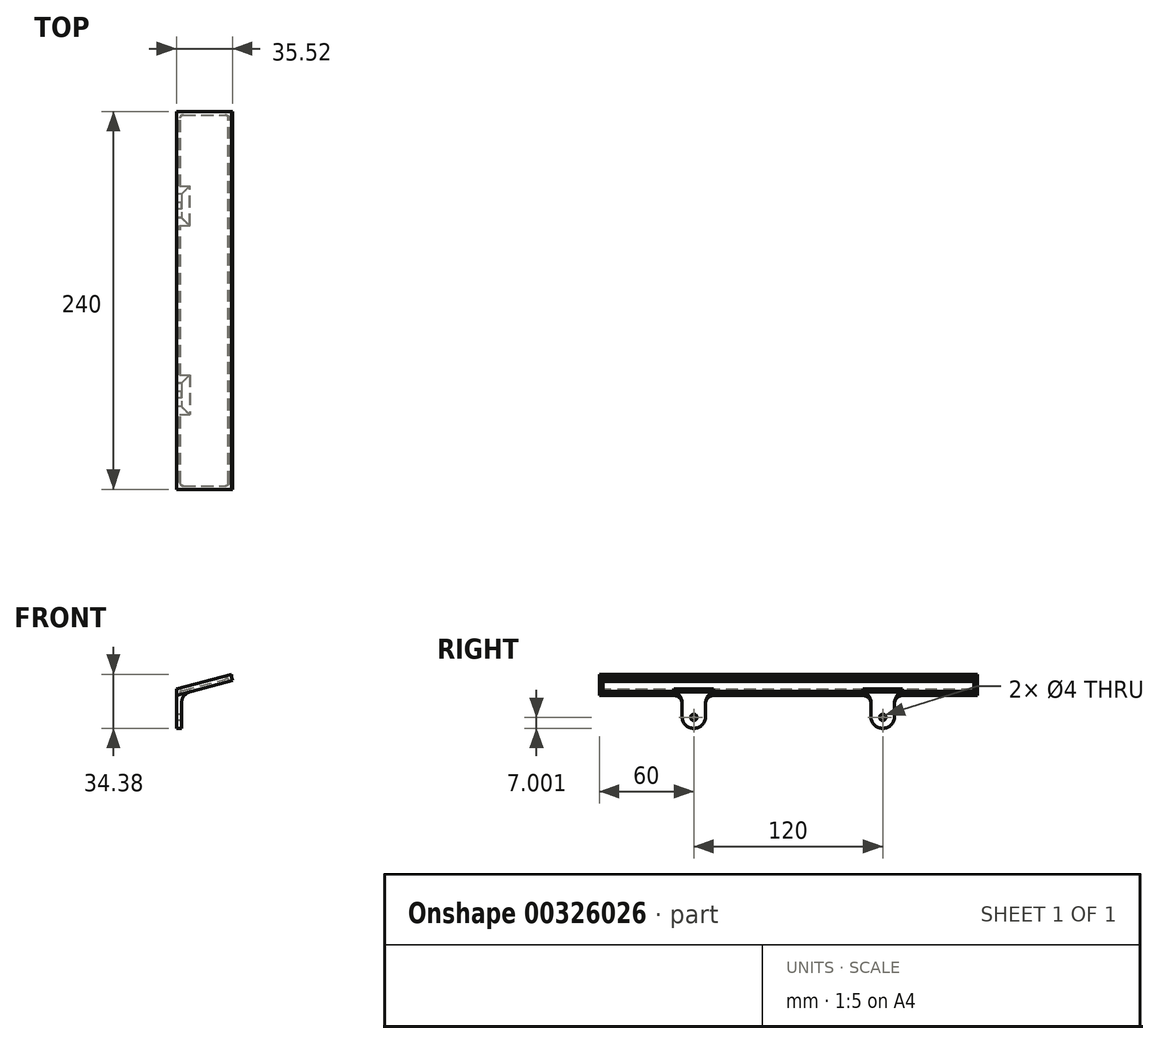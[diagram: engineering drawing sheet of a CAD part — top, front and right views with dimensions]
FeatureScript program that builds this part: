
annotation { "Feature Type Name" : "Feature", "Feature Type Description" : "" }
export const myFeature = defineFeature(function(context is Context, id is Id, definition is map)
    precondition{}
    {
        {
            assignVariable(context, id + "F0", {"name" : "Nozzle", "anyValue" : 1.1});
        }
        {
            var Q0;
            Q0=qCreatedBy(makeId("Front.planeOp"),FACE);
            var sketch = newSketch(context, id + "F1", { "sketchPlane" : qUnion([Q0])});
            skLineSegment(sketch, "E0", {"start": v(0, 2.07) * mm, "end": v(0, 0) * mm});
            skLineSegment(sketch, "E1", {"start": v(0, 0) * mm, "end": v(35, 9.38) * mm});
            skLineSegment(sketch, "E2", {"start": v(35, 9.38) * mm, "end": v(35, 11.45) * mm});
            skLineSegment(sketch, "E3", {"start": v(35, 11.45) * mm, "end": v(0, 2.07) * mm});
            skSolve(sketch);
        }
        {
            var Q0;
            Q0=makeQuery(id+"F1.imprint","IMPRINT",FACE,{"disambiguationData":[TD([[makeQuery(id+"F1.imprint","IMPRINT",EDGE,{"derivedFrom":sQuery(id+"F1.wireOp",EDGE,"E0")}),1.0]])]});
            extrude(context, id + "F2", {"entities" : qUnion([Q0]), "endBound" : BoundingType.SYMMETRIC, "depth" : 240 * mm});
        }
        {
            var Q0;
            Q0=makeQuery(id+"F2.opExtrude","SWEPT_FACE",FACE,{"disambiguationData":[OSD([sQuery(id+"F1.wireOp",EDGE,"E1")])]});
            var sketch = newSketch(context, id + "F3", { "sketchPlane" : qUnion([Q0])});
            skLineSegment(sketch, "E4.0", {"start": v(2.2, 117.8) * mm, "end": v(34.03, 117.8) * mm});
            skLineSegment(sketch, "E4.1", {"start": v(2.2, 117.8) * mm, "end": v(2.2, -117.8) * mm});
            skLineSegment(sketch, "E4.2", {"start": v(2.2, -117.8) * mm, "end": v(34.03, -117.8) * mm});
            skLineSegment(sketch, "E4.3", {"start": v(34.03, 117.8) * mm, "end": v(34.03, -117.8) * mm});
            skLineSegment(sketch, "E5", {"start": v(34.03, 117.8) * mm, "end": v(23.42, 117.8) * mm, "construction": true});
            skLineSegment(sketch, "E6", {"start": v(23.42, 117.8) * mm, "end": v(12.81, 117.8) * mm, "construction": true});
            skLineSegment(sketch, "E7", {"start": v(12.81, 117.8) * mm, "end": v(2.2, 117.8) * mm, "construction": true});
            skLineSegment(sketch, "E8.bottom", {"start": v(29.83, 117.8) * mm, "end": v(27.63, 117.8) * mm});
            skLineSegment(sketch, "E8.top", {"start": v(29.83, -117.8) * mm, "end": v(27.63, -117.8) * mm});
            skLineSegment(sketch, "E8.left", {"start": v(29.83, 117.8) * mm, "end": v(29.83, -117.8) * mm});
            skLineSegment(sketch, "E8.right", {"start": v(27.63, 117.8) * mm, "end": v(27.63, -117.8) * mm});
            skPoint(sketch, "E8.middle", {"position": v(28.73, 0) * mm});
            skPoint(sketch, "E8.middle.positionSnap0", {"position": v(28.73, 117.8) * mm});
            skPoint(sketch, "E8.centerSnap0", {"position": v(28.73, 117.8) * mm});
            skLineSegment(sketch, "E9.bottom", {"start": v(19.22, 117.8) * mm, "end": v(17.02, 117.8) * mm});
            skLineSegment(sketch, "E9.top", {"start": v(19.22, -117.8) * mm, "end": v(17.02, -117.8) * mm});
            skLineSegment(sketch, "E9.left", {"start": v(19.22, 117.8) * mm, "end": v(19.22, -117.8) * mm});
            skLineSegment(sketch, "E9.right", {"start": v(17.02, 117.8) * mm, "end": v(17.02, -117.8) * mm});
            skPoint(sketch, "E9.middle", {"position": v(18.12, 0) * mm});
            skPoint(sketch, "E9.middle.positionSnap0", {"position": v(18.12, 117.8) * mm});
            skPoint(sketch, "E9.centerSnap0", {"position": v(18.12, 117.8) * mm});
            skLineSegment(sketch, "E10.bottom", {"start": v(8.6, 117.8) * mm, "end": v(6.4, 117.8) * mm});
            skLineSegment(sketch, "E10.top", {"start": v(8.6, -117.8) * mm, "end": v(6.4, -117.8) * mm});
            skLineSegment(sketch, "E10.left", {"start": v(8.6, 117.8) * mm, "end": v(8.6, -117.8) * mm});
            skLineSegment(sketch, "E10.right", {"start": v(6.4, 117.8) * mm, "end": v(6.4, -117.8) * mm});
            skPoint(sketch, "E10.middle", {"position": v(7.5, 0) * mm});
            skPoint(sketch, "E10.middle.positionSnap0", {"position": v(7.5, 117.8) * mm});
            skPoint(sketch, "E10.centerSnap0", {"position": v(7.5, 117.8) * mm});
            skSolve(sketch);
        }
        {
            var Q0;
            {var subQ1=sQuery(id+"F3.wireOp",EDGE,"af7b14f9-d1cf-4eca-9090-a69f74b563bf.0");var subQ6=sQuery(id+"F3.wireOp",EDGE,"af7b14f9-d1cf-4eca-9090-a69f74b563bf.1");var subQ9=makeQuery(id+"F3.imprint","INTERSECT",VERTEX,{"derivedFrom":[subQ1,subQ6]});Q0=makeQuery(id+"F3.imprint","IMPRINT",FACE,{"disambiguationData":[TD([[makeQuery(id+"F3.imprint","IMPRINT",EDGE,{"disambiguationData":[TD([[subQ9,-1.0]])],"derivedFrom":subQ1}),-1.0]])]});}
            var Q1;
            {var subQ0=sQuery(id+"F3.wireOp",EDGE,"WsX4oOdL-xhSa-b9M0-yzqE-rsdMtIv8YLiA");var subQ1=sQuery(id+"F3.wireOp",EDGE,"TJxlc4aa-K5Sg-wJQW-KS3G-Ub1AUzvl6ed2");var subQ2=makeQuery(id+"F3.imprint","INTERSECT",VERTEX,{"derivedFrom":[subQ1,subQ0]});Q1=makeQuery(id+"F3.imprint","IMPRINT",FACE,{"disambiguationData":[TD([[makeQuery(id+"F3.imprint","IMPRINT",EDGE,{"disambiguationData":[TD([[subQ2,-1.0]])],"derivedFrom":subQ1}),1.0]])]});}
            var Q2;
            {var subQ5=sQuery(id+"F3.wireOp",EDGE,"af7b14f9-d1cf-4eca-9090-a69f74b563bf.1");var subQ7=sQuery(id+"F3.wireOp",EDGE,"af7b14f9-d1cf-4eca-9090-a69f74b563bf.2");var subQ8=makeQuery(id+"F3.imprint","INTERSECT",VERTEX,{"derivedFrom":[subQ5,subQ7]});Q2=makeQuery(id+"F3.imprint","IMPRINT",FACE,{"disambiguationData":[TD([[makeQuery(id+"F3.imprint","IMPRINT",EDGE,{"disambiguationData":[TD([[subQ8,-1.0]])],"derivedFrom":subQ5}),-1.0]])]});}
            var Q3;
            {var subQ5=sQuery(id+"F3.wireOp",EDGE,"WsX4oOdL-xhSa-b9M0-yzqE-rsdMtIv8YLiA");var subQ6=sQuery(id+"F3.wireOp",EDGE,"af7b14f9-d1cf-4eca-9090-a69f74b563bf.0");var subQ7=makeQuery(id+"F3.imprint","INTERSECT",VERTEX,{"derivedFrom":[subQ6,subQ5]});Q3=makeQuery(id+"F3.imprint","IMPRINT",FACE,{"disambiguationData":[TD([[makeQuery(id+"F3.imprint","IMPRINT",EDGE,{"disambiguationData":[TD([[subQ7,-1.0]])],"derivedFrom":subQ6}),-1.0]])]});}
            var Q4;
            {var subQ32=sQuery(id+"F1.wireOp",EDGE,"E1");Q4=makeQuery(id+"F3.imprint","IMPRINT",FACE,{"disambiguationData":[TD([[makeQuery(id+"F3.imprint","IMPRINT",EDGE,{"derivedFrom":makeQuery(id+"F2.opExtrude","CAP_EDGE",EDGE,{"disambiguationData":[OSD([subQ32])],"isStart":true})}),1.0]])]});}
            var Q5;
            {var subQ5=sQuery(id+"F3.wireOp",EDGE,"TJxlc4aa-K5Sg-wJQW-KS3G-Ub1AUzvl6ed2");var subQ6=sQuery(id+"F3.wireOp",EDGE,"af7b14f9-d1cf-4eca-9090-a69f74b563bf.2");var subQ7=makeQuery(id+"F3.imprint","INTERSECT",VERTEX,{"derivedFrom":[subQ6,subQ5]});Q5=makeQuery(id+"F3.imprint","IMPRINT",FACE,{"disambiguationData":[TD([[makeQuery(id+"F3.imprint","IMPRINT",EDGE,{"disambiguationData":[TD([[subQ7,-1.0]])],"derivedFrom":subQ6}),1.0]])]});}
            var Q6;
            {var subQ9=sQuery(id+"F3.wireOp",EDGE,"82dd6ac8-2e59-40ef-baac-4cfd8f5da2f0.1.0.2");var subQ10=sQuery(id+"F3.wireOp",EDGE,"af7b14f9-d1cf-4eca-9090-a69f74b563bf.0");var subQ11=makeQuery(id+"F3.imprint","INTERSECT",VERTEX,{"derivedFrom":[subQ10,subQ9]});Q6=makeQuery(id+"F3.imprint","IMPRINT",FACE,{"disambiguationData":[TD([[makeQuery(id+"F3.imprint","IMPRINT",EDGE,{"disambiguationData":[TD([[subQ11,-1.0]])],"derivedFrom":subQ10}),-1.0]])]});}
            var Q7;
            {var subQ3=sQuery(id+"F3.wireOp",EDGE,"82dd6ac8-2e59-40ef-baac-4cfd8f5da2f0.1.0.1");var subQ9=sQuery(id+"F3.wireOp",EDGE,"af7b14f9-d1cf-4eca-9090-a69f74b563bf.2");var subQ10=makeQuery(id+"F3.imprint","INTERSECT",VERTEX,{"derivedFrom":[subQ9,subQ3]});Q7=makeQuery(id+"F3.imprint","IMPRINT",FACE,{"disambiguationData":[TD([[makeQuery(id+"F3.imprint","IMPRINT",EDGE,{"disambiguationData":[TD([[subQ10,-1.0]])],"derivedFrom":subQ9}),1.0]])]});}
            var Q8;
            {var subQ0=sQuery(id+"F3.wireOp",EDGE,"82dd6ac8-2e59-40ef-baac-4cfd8f5da2f0.1.0.3");var subQ1=sQuery(id+"F3.wireOp",EDGE,"82dd6ac8-2e59-40ef-baac-4cfd8f5da2f0.1.0.0");var subQ2=makeQuery(id+"F3.imprint","INTERSECT",VERTEX,{"derivedFrom":[subQ1,subQ0]});Q8=makeQuery(id+"F3.imprint","IMPRINT",FACE,{"disambiguationData":[TD([[makeQuery(id+"F3.imprint","IMPRINT",EDGE,{"disambiguationData":[TD([[subQ2,-1.0]])],"derivedFrom":subQ1}),1.0]])]});}
            var Q9;
            {var subQ0=sQuery(id+"F3.wireOp",EDGE,"3767ce86-fc12-45c4-ae98-b7fda9e548f23.MirrorCS");var subQ1=sQuery(id+"F3.wireOp",EDGE,"af7b14f9-d1cf-4eca-9090-a69f74b563bf.0");var subQ2=makeQuery(id+"F3.imprint","INTERSECT",VERTEX,{"derivedFrom":[subQ1,subQ0]});Q9=makeQuery(id+"F3.imprint","IMPRINT",FACE,{"disambiguationData":[TD([[makeQuery(id+"F3.imprint","IMPRINT",EDGE,{"disambiguationData":[TD([[subQ2,-1.0]])],"derivedFrom":subQ1}),-1.0]])]});}
            var Q10;
            {var subQ1=sQuery(id+"F3.wireOp",EDGE,"3767ce86-fc12-45c4-ae98-b7fda9e548f20.MirrorCS");var subQ9=sQuery(id+"F3.wireOp",EDGE,"af7b14f9-d1cf-4eca-9090-a69f74b563bf.2");var subQ10=makeQuery(id+"F3.imprint","INTERSECT",VERTEX,{"derivedFrom":[subQ9,subQ1]});Q10=makeQuery(id+"F3.imprint","IMPRINT",FACE,{"disambiguationData":[TD([[makeQuery(id+"F3.imprint","IMPRINT",EDGE,{"disambiguationData":[TD([[subQ10,-1.0]])],"derivedFrom":subQ9}),1.0]])]});}
            var Q11;
            {var subQ5=sQuery(id+"F3.wireOp",EDGE,"af7b14f9-d1cf-4eca-9090-a69f74b563bf.0");var subQ7=sQuery(id+"F3.wireOp",EDGE,"af7b14f9-d1cf-4eca-9090-a69f74b563bf.3");var subQ8=makeQuery(id+"F3.imprint","INTERSECT",VERTEX,{"derivedFrom":[subQ5,subQ7]});Q11=makeQuery(id+"F3.imprint","IMPRINT",FACE,{"disambiguationData":[TD([[makeQuery(id+"F3.imprint","IMPRINT",EDGE,{"disambiguationData":[TD([[subQ8,1.0]])],"derivedFrom":subQ5}),-1.0]])]});}
            var Q12;
            {var subQ0=sQuery(id+"F3.wireOp",EDGE,"af7b14f9-d1cf-4eca-9090-a69f74b563bf.3");var subQ1=sQuery(id+"F3.wireOp",EDGE,"af7b14f9-d1cf-4eca-9090-a69f74b563bf.2");var subQ2=makeQuery(id+"F3.imprint","INTERSECT",VERTEX,{"derivedFrom":[subQ1,subQ0]});Q12=makeQuery(id+"F3.imprint","IMPRINT",FACE,{"disambiguationData":[TD([[makeQuery(id+"F3.imprint","IMPRINT",EDGE,{"disambiguationData":[TD([[subQ2,1.0]])],"derivedFrom":subQ1}),1.0]])]});}
            var Q13;
            {var subQ0=sQuery(id+"F3.wireOp",EDGE,"3767ce86-fc12-45c4-ae98-b7fda9e548f27.MirrorCS");var subQ1=sQuery(id+"F3.wireOp",EDGE,"3767ce86-fc12-45c4-ae98-b7fda9e548f24.MirrorCS");var subQ2=makeQuery(id+"F3.imprint","INTERSECT",VERTEX,{"derivedFrom":[subQ1,subQ0]});Q13=makeQuery(id+"F3.imprint","IMPRINT",FACE,{"disambiguationData":[TD([[makeQuery(id+"F3.imprint","IMPRINT",EDGE,{"disambiguationData":[TD([[subQ2,-1.0]])],"derivedFrom":subQ1}),-1.0]])]});}
            var Q14;
            {var subQ0=sQuery(id+"F3.wireOp",EDGE,"3767ce86-fc12-45c4-ae98-b7fda9e548f22.MirrorCS");var subQ1=sQuery(id+"F3.wireOp",EDGE,"3767ce86-fc12-45c4-ae98-b7fda9e548f20.MirrorCS");var subQ2=makeQuery(id+"F3.imprint","INTERSECT",VERTEX,{"derivedFrom":[subQ1,subQ0]});Q14=makeQuery(id+"F3.imprint","IMPRINT",FACE,{"disambiguationData":[TD([[makeQuery(id+"F3.imprint","IMPRINT",EDGE,{"disambiguationData":[TD([[subQ2,-1.0]])],"derivedFrom":subQ1}),-1.0]])]});}
            var Q15;
            {var subQ32=sQuery(id+"F3.wireOp",EDGE,"271a5217-1f75-4fcf-8b44-c3014ae48224.0");Q15=makeQuery(id+"F3.imprint","IMPRINT",FACE,{"disambiguationData":[TD([[makeQuery(id+"F3.imprint","IMPRINT",EDGE,{"derivedFrom":subQ32}),1.0]])]});}
            var Q16;
            Q16=makeQuery(id+"F3.imprint","IMPRINT",FACE,{"disambiguationData":[TD([[makeQuery(id+"F3.imprint","IMPRINT",EDGE,{"derivedFrom":sQuery(id+"F3.wireOp",EDGE,"E8.bottom")}),1.0]])]});
            var Q17;
            Q17=makeQuery(id+"F3.imprint","IMPRINT",FACE,{"disambiguationData":[TD([[makeQuery(id+"F3.imprint","IMPRINT",EDGE,{"derivedFrom":sQuery(id+"F3.wireOp",EDGE,"E9.bottom")}),1.0]])]});
            var Q18;
            Q18=makeQuery(id+"F3.imprint","IMPRINT",FACE,{"disambiguationData":[TD([[makeQuery(id+"F3.imprint","IMPRINT",EDGE,{"derivedFrom":sQuery(id+"F3.wireOp",EDGE,"E10.bottom")}),1.0]])]});
            extrude(context, id + "F4", {"entities" : qUnion([Q0, Q1, Q2, Q3, Q4, Q5, Q6, Q7, Q8, Q9, Q10, Q11, Q12, Q13, Q14, Q15, Q16, Q17, Q18]), "operationType" : NewBodyOperationType.ADD, "depth" : 2 * mm});
        }
        {
            var Q0;
            Q0=makeQuery(id+"F4.opExtrude","SWEPT_EDGE",EDGE,{"disambiguationData":[OSD([sQuery(id+"F3.wireOp",EDGE,"E4.0"),sQuery(id+"F3.wireOp",EDGE,"E4.3")])]});
            var Q1;
            Q1=makeQuery(id+"F4.opExtrude","SWEPT_EDGE",EDGE,{"disambiguationData":[OSD([sQuery(id+"F3.wireOp",EDGE,"E4.0"),sQuery(id+"F3.wireOp",EDGE,"E8.bottom"),sQuery(id+"F3.wireOp",EDGE,"E8.right")])]});
            var Q2;
            Q2=makeQuery(id+"F4.opExtrude","SWEPT_EDGE",EDGE,{"disambiguationData":[OSD([sQuery(id+"F3.wireOp",EDGE,"E4.0"),sQuery(id+"F3.wireOp",EDGE,"E9.bottom"),sQuery(id+"F3.wireOp",EDGE,"E9.right")])]});
            var Q3;
            Q3=makeQuery(id+"F4.opExtrude","SWEPT_EDGE",EDGE,{"disambiguationData":[OSD([sQuery(id+"F3.wireOp",EDGE,"E4.0"),sQuery(id+"F3.wireOp",EDGE,"E10.bottom"),sQuery(id+"F3.wireOp",EDGE,"E10.right")])]});
            var Q4;
            Q4=makeQuery(id+"F4.opExtrude","SWEPT_EDGE",EDGE,{"disambiguationData":[OSD([sQuery(id+"F3.wireOp",EDGE,"E4.0"),sQuery(id+"F3.wireOp",EDGE,"E8.bottom"),sQuery(id+"F3.wireOp",EDGE,"E8.left")])]});
            var Q5;
            Q5=makeQuery(id+"F4.opExtrude","SWEPT_EDGE",EDGE,{"disambiguationData":[OSD([sQuery(id+"F3.wireOp",EDGE,"E4.0"),sQuery(id+"F3.wireOp",EDGE,"E9.bottom"),sQuery(id+"F3.wireOp",EDGE,"E9.left")])]});
            var Q6;
            Q6=makeQuery(id+"F4.opExtrude","SWEPT_EDGE",EDGE,{"disambiguationData":[OSD([sQuery(id+"F3.wireOp",EDGE,"E4.0"),sQuery(id+"F3.wireOp",EDGE,"E10.bottom"),sQuery(id+"F3.wireOp",EDGE,"E10.left")])]});
            var Q7;
            Q7=makeQuery(id+"F4.opExtrude","SWEPT_EDGE",EDGE,{"disambiguationData":[OSD([sQuery(id+"F3.wireOp",EDGE,"E4.0"),sQuery(id+"F3.wireOp",EDGE,"E4.1")])]});
            var Q8;
            Q8=makeQuery(id+"F4.opExtrude","SWEPT_EDGE",EDGE,{"disambiguationData":[OSD([sQuery(id+"F3.wireOp",EDGE,"E4.1"),sQuery(id+"F3.wireOp",EDGE,"E4.2")])]});
            var Q9;
            Q9=makeQuery(id+"F4.opExtrude","SWEPT_EDGE",EDGE,{"disambiguationData":[OSD([sQuery(id+"F3.wireOp",EDGE,"E4.2"),sQuery(id+"F3.wireOp",EDGE,"E10.top"),sQuery(id+"F3.wireOp",EDGE,"E10.left")])]});
            var Q10;
            Q10=makeQuery(id+"F4.opExtrude","SWEPT_EDGE",EDGE,{"disambiguationData":[OSD([sQuery(id+"F3.wireOp",EDGE,"E4.2"),sQuery(id+"F3.wireOp",EDGE,"E9.top"),sQuery(id+"F3.wireOp",EDGE,"E9.left")])]});
            var Q11;
            Q11=makeQuery(id+"F4.opExtrude","SWEPT_EDGE",EDGE,{"disambiguationData":[OSD([sQuery(id+"F3.wireOp",EDGE,"E4.2"),sQuery(id+"F3.wireOp",EDGE,"E8.top"),sQuery(id+"F3.wireOp",EDGE,"E8.left")])]});
            var Q12;
            Q12=makeQuery(id+"F4.opExtrude","SWEPT_EDGE",EDGE,{"disambiguationData":[OSD([sQuery(id+"F3.wireOp",EDGE,"E4.2"),sQuery(id+"F3.wireOp",EDGE,"E4.3")])]});
            var Q13;
            Q13=makeQuery(id+"F4.opExtrude","SWEPT_EDGE",EDGE,{"disambiguationData":[OSD([sQuery(id+"F3.wireOp",EDGE,"E4.2"),sQuery(id+"F3.wireOp",EDGE,"E9.top"),sQuery(id+"F3.wireOp",EDGE,"E9.right")])]});
            var Q14;
            Q14=makeQuery(id+"F4.opExtrude","SWEPT_EDGE",EDGE,{"disambiguationData":[OSD([sQuery(id+"F3.wireOp",EDGE,"E4.2"),sQuery(id+"F3.wireOp",EDGE,"E10.top"),sQuery(id+"F3.wireOp",EDGE,"E10.right")])]});
            var Q15;
            Q15=makeQuery(id+"F4.opExtrude","SWEPT_EDGE",EDGE,{"disambiguationData":[OSD([sQuery(id+"F3.wireOp",EDGE,"E4.2"),sQuery(id+"F3.wireOp",EDGE,"E8.top"),sQuery(id+"F3.wireOp",EDGE,"E8.right")])]});
            fillet(context, id + "F5", {"entities" : qUnion([Q0, Q1, Q2, Q3, Q4, Q5, Q6, Q7, Q8, Q9, Q10, Q11, Q12, Q13, Q14, Q15]), "radius" : 2 * mm, "tangentPropagation" : true, "allowEdgeOverflow" : false});
        }
        {
            var Q0;
            {var subQ0=sQuery(id+"F1.wireOp",EDGE,"E1");var subQ1=makeQuery(id+"F2.opExtrude","CAP_EDGE",EDGE,{"disambiguationData":[OSD([subQ0])],"isStart":false});var subQ2=sQuery(id+"F1.wireOp",EDGE,"E2");var subQ3=makeQuery(id+"F3.imprint","INTERSECT",VERTEX,{"derivedFrom":[subQ1,sQuery(id+"F3.wireOp",EDGE,"271a5217-1f75-4fcf-8b44-c3014ae48224.0")]});Q0=makeQuery(id+"F4.boolean.opBoolean","MERGE",FACE,{"derivedFrom":[makeQuery(id+"F2.opExtrude","CAP_FACE",FACE,{"disambiguationData":[OSD([sQuery(id+"F1.wireOp",EDGE,"E0"),subQ0,subQ2,sQuery(id+"F1.wireOp",EDGE,"E3")])],"isStart":false}),makeQuery(id+"F4.opExtrude","SWEPT_FACE",FACE,{"disambiguationData":[OSD([subQ0]),TDD([makeQuery(id+"F3.imprint","IMPRINT",EDGE,{"disambiguationData":[TD([[makeQuery(id+"F3.imprint","INTERSECT",VERTEX,{"derivedFrom":[subQ1,sQuery(id+"F3.wireOp",EDGE,"450e035a-21f1-4329-b4e3-3c460cd04c57.0")]}),-1.0]])],"derivedFrom":subQ1}),makeQuery(id+"F3.imprint","IMPRINT",EDGE,{"disambiguationData":[TD([[subQ3,-1.0]])],"derivedFrom":subQ1})])]})]});}
            var sketch = newSketch(context, id + "F6", { "sketchPlane" : qUnion([Q0])});
            skLineSegment(sketch, "E11.0", {"start": v(0.52, -1.93) * mm, "end": v(0, 0) * mm});
            skLineSegment(sketch, "E12", {"start": v(0, 0) * mm, "end": v(0, -2.07) * mm});
            skLineSegment(sketch, "E13", {"start": v(0.52, -1.93) * mm, "end": v(0, -2.07) * mm});
            skSolve(sketch);
        }
        {
            var Q0;
            Q0=makeQuery(id+"F6.imprint","IMPRINT",FACE,{"disambiguationData":[TD([[makeQuery(id+"F6.imprint","IMPRINT",EDGE,{"derivedFrom":sQuery(id+"F6.wireOp",EDGE,"E11.0")}),1.0]])]});
            var Q1;
            {var subQ0=sQuery(id+"F1.wireOp",EDGE,"E1");var subQ1=makeQuery(id+"F2.opExtrude","CAP_EDGE",EDGE,{"disambiguationData":[OSD([subQ0])],"isStart":true});var subQ2=sQuery(id+"F1.wireOp",EDGE,"E2");var subQ3=makeQuery(id+"F3.imprint","INTERSECT",VERTEX,{"derivedFrom":[subQ1,sQuery(id+"F3.wireOp",EDGE,"271a5217-1f75-4fcf-8b44-c3014ae48224.0")]});Q1=makeQuery(id+"F4.boolean.opBoolean","MERGE",FACE,{"derivedFrom":[makeQuery(id+"F2.opExtrude","CAP_FACE",FACE,{"disambiguationData":[OSD([sQuery(id+"F1.wireOp",EDGE,"E0"),subQ0,subQ2,sQuery(id+"F1.wireOp",EDGE,"E3")])],"isStart":true}),makeQuery(id+"F4.opExtrude","SWEPT_FACE",FACE,{"disambiguationData":[OSD([subQ0]),TDD([makeQuery(id+"F3.imprint","IMPRINT",EDGE,{"disambiguationData":[TD([[makeQuery(id+"F3.imprint","INTERSECT",VERTEX,{"derivedFrom":[subQ1,sQuery(id+"F3.wireOp",EDGE,"450e035a-21f1-4329-b4e3-3c460cd04c57.0")]}),-1.0]])],"derivedFrom":subQ1}),makeQuery(id+"F3.imprint","IMPRINT",EDGE,{"disambiguationData":[TD([[subQ3,-1.0]])],"derivedFrom":subQ1})])]})]});}
            extrude(context, id + "F7", {"entities" : qUnion([Q0]), "operationType" : NewBodyOperationType.ADD, "endBound" : BoundingType.UP_TO_SURFACE, "oppositeDirection" : true, "endBoundEntityFace" : qUnion([Q1]), "depth" : 25 * mm});
        }
        {
            var Q0;
            Q0=makeQuery(id+"F2.opExtrude","SWEPT_FACE",FACE,{"disambiguationData":[OSD([sQuery(id+"F1.wireOp",EDGE,"E0")])]});
            var sketch = newSketch(context, id + "F8", { "sketchPlane" : qUnion([Q0])});
            skLineSegment(sketch, "E14.top", {"start": v(-67.5, -22.93) * mm, "end": v(-52.5, -22.93) * mm});
            skLineSegment(sketch, "E14.right", {"start": v(-52.5, 2.07) * mm, "end": v(-52.5, -22.93) * mm});
            skCircle(sketch, "E15", {"center": v(-60, -15.93) * mm, "radius": 2 * mm});
            skPoint(sketch, "E15.centerSnap0", {"position": v(-60, -22.93) * mm});
            skLineSegment(sketch, "E16", {"start": v(-67.5, -22.93) * mm, "end": v(-67.5, 2.07) * mm});
            skLineSegment(sketch, "E17", {"start": v(-67.5, 2.07) * mm, "end": v(-52.5, 2.07) * mm});
            skPoint(sketch, "E18.MirrorP", {"position": v(60, -22.93) * mm});
            skLineSegment(sketch, "E19.MirrorCS", {"start": v(67.5, -22.93) * mm, "end": v(67.5, 2.07) * mm});
            skLineSegment(sketch, "E20.MirrorCS", {"start": v(67.5, 2.07) * mm, "end": v(52.5, 2.07) * mm});
            skLineSegment(sketch, "E21.MirrorCS", {"start": v(52.5, 2.07) * mm, "end": v(52.5, -22.93) * mm});
            skLineSegment(sketch, "E22.MirrorCS", {"start": v(67.5, -22.93) * mm, "end": v(52.5, -22.93) * mm});
            skCircle(sketch, "E23.MirrorC", {"center": v(60, -15.93) * mm, "radius": 2 * mm});
            skLineSegment(sketch, "E24", {"start": v(0, 0) * mm, "end": v(-120, 2.07) * mm, "construction": true});
            skLineSegment(sketch, "E25", {"start": v(-60, -22.93) * mm, "end": v(-60, 1.04) * mm, "construction": true});
            skSolve(sketch);
        }
        {
            var Q0;
            {var subQ0=sQuery(id+"F8.wireOp",EDGE,"E17");Q0=makeQuery(id+"F8.imprint","IMPRINT",FACE,{"disambiguationData":[TD([[makeQuery(id+"F8.imprint","IMPRINT",EDGE,{"derivedFrom":subQ0}),1.0]])]});}
            var Q1;
            {var subQ1=sQuery(id+"F8.wireOp",EDGE,"E14.top");Q1=makeQuery(id+"F8.imprint","IMPRINT",FACE,{"disambiguationData":[TD([[makeQuery(id+"F8.imprint","IMPRINT",EDGE,{"derivedFrom":subQ1}),1.0]])]});}
            var Q2;
            {var subQ0=sQuery(id+"F8.wireOp",EDGE,"E20.MirrorCS");Q2=makeQuery(id+"F8.imprint","IMPRINT",FACE,{"disambiguationData":[TD([[makeQuery(id+"F8.imprint","IMPRINT",EDGE,{"derivedFrom":subQ0}),1.0]])]});}
            var Q3;
            {var subQ0=sQuery(id+"F8.wireOp",EDGE,"E22.MirrorCS");Q3=makeQuery(id+"F8.imprint","IMPRINT",FACE,{"disambiguationData":[TD([[makeQuery(id+"F8.imprint","IMPRINT",EDGE,{"derivedFrom":subQ0}),-1.0]])]});}
            extrude(context, id + "F9", {"entities" : qUnion([Q0, Q1, Q2, Q3]), "operationType" : NewBodyOperationType.ADD, "oppositeDirection" : true, "depth" : (getVariable(context, 'Nozzle') * 3) * mm});
        }
        {
            var Q0;
            Q0=makeQuery(id+"F9.opExtrude","SWEPT_EDGE",EDGE,{"disambiguationData":[OSD([sQuery(id+"F8.wireOp",EDGE,"E14.top"),sQuery(id+"F8.wireOp",EDGE,"E16")])]});
            var Q1;
            Q1=makeQuery(id+"F9.opExtrude","SWEPT_EDGE",EDGE,{"disambiguationData":[OSD([sQuery(id+"F8.wireOp",EDGE,"E14.top"),sQuery(id+"F8.wireOp",EDGE,"E14.right")])]});
            var Q2;
            Q2=makeQuery(id+"F9.opExtrude","SWEPT_EDGE",EDGE,{"disambiguationData":[OSD([sQuery(id+"F8.wireOp",EDGE,"E21.MirrorCS"),sQuery(id+"F8.wireOp",EDGE,"E22.MirrorCS")])]});
            var Q3;
            Q3=makeQuery(id+"F9.opExtrude","SWEPT_EDGE",EDGE,{"disambiguationData":[OSD([sQuery(id+"F8.wireOp",EDGE,"E19.MirrorCS"),sQuery(id+"F8.wireOp",EDGE,"E22.MirrorCS")])]});
            fillet(context, id + "F10", {"entities" : qUnion([Q0, Q1, Q2, Q3]), "radius" : 7.5 * mm, "tangentPropagation" : true, "allowEdgeOverflow" : false});
        }
        {
            var Q0;
            Q0=makeQuery(id+"F7.boolean.opBoolean","MERGE",FACE,{"derivedFrom":[makeQuery(id+"F4.opExtrude","CAP_FACE",FACE,{"disambiguationData":[OSD([sQuery(id+"F1.wireOp",EDGE,"E1"),sQuery(id+"F1.wireOp",EDGE,"E2"),sQuery(id+"F3.wireOp",EDGE,"af7b14f9-d1cf-4eca-9090-a69f74b563bf.0"),sQuery(id+"F3.wireOp",EDGE,"af7b14f9-d1cf-4eca-9090-a69f74b563bf.1"),sQuery(id+"F3.wireOp",EDGE,"af7b14f9-d1cf-4eca-9090-a69f74b563bf.2"),sQuery(id+"F3.wireOp",EDGE,"af7b14f9-d1cf-4eca-9090-a69f74b563bf.3"),sQuery(id+"F3.wireOp",EDGE,"TJxlc4aa-K5Sg-wJQW-KS3G-Ub1AUzvl6ed2"),sQuery(id+"F3.wireOp",EDGE,"snlChxqo-O0Aw-AI0F-VWmB-b1vkiBQb3jRh"),sQuery(id+"F3.wireOp",EDGE,"WsX4oOdL-xhSa-b9M0-yzqE-rsdMtIv8YLiA"),sQuery(id+"F3.wireOp",EDGE,"syYVYZvS-mxP5-lLkx-pa4y-P31EPd25eTEd"),sQuery(id+"F3.wireOp",EDGE,"82dd6ac8-2e59-40ef-baac-4cfd8f5da2f0.1.0.0"),sQuery(id+"F3.wireOp",EDGE,"82dd6ac8-2e59-40ef-baac-4cfd8f5da2f0.1.0.1"),sQuery(id+"F3.wireOp",EDGE,"82dd6ac8-2e59-40ef-baac-4cfd8f5da2f0.1.0.2"),sQuery(id+"F3.wireOp",EDGE,"82dd6ac8-2e59-40ef-baac-4cfd8f5da2f0.1.0.3"),sQuery(id+"F3.wireOp",EDGE,"3767ce86-fc12-45c4-ae98-b7fda9e548f20.MirrorCS"),sQuery(id+"F3.wireOp",EDGE,"3767ce86-fc12-45c4-ae98-b7fda9e548f21.MirrorCS"),sQuery(id+"F3.wireOp",EDGE,"3767ce86-fc12-45c4-ae98-b7fda9e548f22.MirrorCS"),sQuery(id+"F3.wireOp",EDGE,"3767ce86-fc12-45c4-ae98-b7fda9e548f23.MirrorCS"),sQuery(id+"F3.wireOp",EDGE,"3767ce86-fc12-45c4-ae98-b7fda9e548f24.MirrorCS"),sQuery(id+"F3.wireOp",EDGE,"3767ce86-fc12-45c4-ae98-b7fda9e548f25.MirrorCS"),sQuery(id+"F3.wireOp",EDGE,"3767ce86-fc12-45c4-ae98-b7fda9e548f26.MirrorCS"),sQuery(id+"F3.wireOp",EDGE,"3767ce86-fc12-45c4-ae98-b7fda9e548f27.MirrorCS"),sQuery(id+"F3.wireOp",EDGE,"450e035a-21f1-4329-b4e3-3c460cd04c57.0")])],"isStart":false}),makeQuery(id+"F7.opExtrude","SWEPT_FACE",FACE,{"disambiguationData":[OSD([sQuery(id+"F6.wireOp",EDGE,"E13")])]})]});
            var sketch = newSketch(context, id + "F11", { "sketchPlane" : qUnion([Q0])});
            skLineSegment(sketch, "E26.bottom", {"start": v(2.2, -47.49) * mm, "end": v(8.6, -47.49) * mm});
            skLineSegment(sketch, "E26.top", {"start": v(2.2, -72.5) * mm, "end": v(8.6, -72.5) * mm});
            skLineSegment(sketch, "E26.left", {"start": v(2.2, -47.5) * mm, "end": v(2.2, -72.5) * mm});
            skLineSegment(sketch, "E26.right", {"start": v(8.6, -47.49) * mm, "end": v(8.6, -72.5) * mm});
            skLineSegment(sketch, "E27.MirrorCS", {"start": v(2.2, 47.49) * mm, "end": v(8.6, 47.49) * mm});
            skLineSegment(sketch, "E28.MirrorCS", {"start": v(2.2, 72.5) * mm, "end": v(8.6, 72.5) * mm});
            skLineSegment(sketch, "E29.MirrorCS", {"start": v(8.6, 47.49) * mm, "end": v(8.6, 72.5) * mm});
            skLineSegment(sketch, "E30.MirrorCS", {"start": v(2.2, 47.5) * mm, "end": v(2.2, 72.5) * mm});
            skSolve(sketch);
        }
        {
            var Q0;
            {var subQ3=sQuery(id+"F3.wireOp",EDGE,"E10.right");var subQ9=sQuery(id+"F11.wireOp",EDGE,"E26.bottom");var subQ17=makeQuery(id+"F4.opExtrude","CAP_EDGE",EDGE,{"disambiguationData":[OSD([subQ3])],"isStart":false});var subQ19=makeQuery(id+"F11.imprint","INTERSECT",VERTEX,{"derivedFrom":[subQ17,subQ9]});Q0=makeQuery(id+"F11.imprint","IMPRINT",FACE,{"disambiguationData":[TD([[makeQuery(id+"F11.imprint","IMPRINT",EDGE,{"disambiguationData":[TD([[subQ19,-1.0]])],"derivedFrom":subQ17}),-1.0]])]});}
            var Q1;
            {var subQ0=sQuery(id+"F11.wireOp",EDGE,"E26.bottom");var subQ1=makeQuery(id+"F4.opExtrude","CAP_EDGE",EDGE,{"disambiguationData":[OSD([sQuery(id+"F3.wireOp",EDGE,"E10.right")])],"isStart":false});var subQ2=makeQuery(id+"F11.imprint","INTERSECT",VERTEX,{"derivedFrom":[subQ1,subQ0]});Q1=makeQuery(id+"F11.imprint","IMPRINT",FACE,{"disambiguationData":[TD([[makeQuery(id+"F11.imprint","IMPRINT",EDGE,{"disambiguationData":[TD([[subQ2,-1.0]])],"derivedFrom":subQ0}),-1.0]])]});}
            var Q2;
            {var subQ0=sQuery(id+"F11.wireOp",EDGE,"E26.right");Q2=makeQuery(id+"F11.imprint","IMPRINT",FACE,{"disambiguationData":[TD([[makeQuery(id+"F11.imprint","IMPRINT",EDGE,{"derivedFrom":subQ0}),-1.0]])]});}
            var Q3;
            {var subQ3=sQuery(id+"F3.wireOp",EDGE,"E10.right");var subQ15=makeQuery(id+"F4.opExtrude","CAP_EDGE",EDGE,{"disambiguationData":[OSD([subQ3])],"isStart":false});var subQ17=sQuery(id+"F11.wireOp",EDGE,"E27.MirrorCS");var subQ19=makeQuery(id+"F11.imprint","INTERSECT",VERTEX,{"derivedFrom":[subQ15,subQ17]});Q3=makeQuery(id+"F11.imprint","IMPRINT",FACE,{"disambiguationData":[TD([[makeQuery(id+"F11.imprint","IMPRINT",EDGE,{"disambiguationData":[TD([[subQ19,1.0]])],"derivedFrom":subQ15}),-1.0]])]});}
            var Q4;
            {var subQ0=sQuery(id+"F11.wireOp",EDGE,"E27.MirrorCS");var subQ1=makeQuery(id+"F4.opExtrude","CAP_EDGE",EDGE,{"disambiguationData":[OSD([sQuery(id+"F3.wireOp",EDGE,"E10.right")])],"isStart":false});var subQ2=makeQuery(id+"F11.imprint","INTERSECT",VERTEX,{"derivedFrom":[subQ1,subQ0]});Q4=makeQuery(id+"F11.imprint","IMPRINT",FACE,{"disambiguationData":[TD([[makeQuery(id+"F11.imprint","IMPRINT",EDGE,{"disambiguationData":[TD([[subQ2,-1.0]])],"derivedFrom":subQ0}),1.0]])]});}
            var Q5;
            {var subQ0=sQuery(id+"F3.wireOp",EDGE,"E4.1");Q5=makeQuery(id+"F4.boolean.opBoolean","SPLIT",FACE,{"disambiguationData":[TD([makeQuery(id+"F4.opExtrude","SWEPT_FACE",FACE,{"disambiguationData":[OSD([subQ0])]})])],"derivedFrom":makeQuery(id+"F2.opExtrude","SWEPT_FACE",FACE,{"disambiguationData":[OSD([sQuery(id+"F1.wireOp",EDGE,"E1")])]})});}
            extrude(context, id + "F12", {"entities" : qUnion([Q0, Q1, Q2, Q3, Q4]), "operationType" : NewBodyOperationType.ADD, "endBound" : BoundingType.UP_TO_SURFACE, "oppositeDirection" : true, "endBoundEntityFace" : qUnion([Q5]), "depth" : 25 * mm});
        }
        {
            var Q0;
            Q0=makeQuery(id+"F12.boolean.opBoolean","INTERSECT",EDGE,{"derivedFrom":[makeQuery(id+"F9.opExtrude","SWEPT_FACE",FACE,{"disambiguationData":[OSD([sQuery(id+"F8.wireOp",EDGE,"E21.MirrorCS")])]}),makeQuery(id+"F12.opExtrude","CAP_FACE",FACE,{"disambiguationData":[OSD([sQuery(id+"F11.wireOp",EDGE,"E27.MirrorCS"),sQuery(id+"F11.wireOp",EDGE,"E28.MirrorCS"),sQuery(id+"F11.wireOp",EDGE,"E29.MirrorCS"),sQuery(id+"F11.wireOp",EDGE,"E30.MirrorCS")])],"isStart":true})]});
            var Q1;
            Q1=makeQuery(id+"F12.boolean.opBoolean","INTERSECT",EDGE,{"derivedFrom":[makeQuery(id+"F9.opExtrude","SWEPT_FACE",FACE,{"disambiguationData":[OSD([sQuery(id+"F8.wireOp",EDGE,"E19.MirrorCS")])]}),makeQuery(id+"F12.opExtrude","CAP_FACE",FACE,{"disambiguationData":[OSD([sQuery(id+"F11.wireOp",EDGE,"E27.MirrorCS"),sQuery(id+"F11.wireOp",EDGE,"E28.MirrorCS"),sQuery(id+"F11.wireOp",EDGE,"E29.MirrorCS"),sQuery(id+"F11.wireOp",EDGE,"E30.MirrorCS")])],"isStart":true})]});
            var Q2;
            Q2=makeQuery(id+"F12.boolean.opBoolean","INTERSECT",EDGE,{"derivedFrom":[makeQuery(id+"F9.opExtrude","SWEPT_FACE",FACE,{"disambiguationData":[OSD([sQuery(id+"F8.wireOp",EDGE,"E14.right")])]}),makeQuery(id+"F12.opExtrude","CAP_FACE",FACE,{"disambiguationData":[OSD([sQuery(id+"F11.wireOp",EDGE,"E26.bottom"),sQuery(id+"F11.wireOp",EDGE,"E26.top"),sQuery(id+"F11.wireOp",EDGE,"E26.left"),sQuery(id+"F11.wireOp",EDGE,"E26.right")])],"isStart":true})]});
            var Q3;
            Q3=makeQuery(id+"F12.boolean.opBoolean","INTERSECT",EDGE,{"derivedFrom":[makeQuery(id+"F9.opExtrude","SWEPT_FACE",FACE,{"disambiguationData":[OSD([sQuery(id+"F8.wireOp",EDGE,"E16")])]}),makeQuery(id+"F12.opExtrude","CAP_FACE",FACE,{"disambiguationData":[OSD([sQuery(id+"F11.wireOp",EDGE,"E26.bottom"),sQuery(id+"F11.wireOp",EDGE,"E26.top"),sQuery(id+"F11.wireOp",EDGE,"E26.left"),sQuery(id+"F11.wireOp",EDGE,"E26.right")])],"isStart":true})]});
            fillet(context, id + "F13", {"entities" : qUnion([Q0, Q1, Q2, Q3]), "radius" : 5 * mm, "tangentPropagation" : true, "allowEdgeOverflow" : false});
        }
        {
            var Q0;
            Q0=makeQuery(id+"F12.boolean.opBoolean","INTERSECT",EDGE,{"derivedFrom":[makeQuery(id+"F9.opExtrude","CAP_FACE",FACE,{"disambiguationData":[OSD([sQuery(id+"F8.wireOp",EDGE,"E14.top"),sQuery(id+"F8.wireOp",EDGE,"E14.right"),sQuery(id+"F8.wireOp",EDGE,"E15"),sQuery(id+"F8.wireOp",EDGE,"E16"),sQuery(id+"F8.wireOp",EDGE,"E17")])],"isStart":false}),makeQuery(id+"F12.opExtrude","CAP_FACE",FACE,{"disambiguationData":[OSD([sQuery(id+"F11.wireOp",EDGE,"E26.bottom"),sQuery(id+"F11.wireOp",EDGE,"E26.top"),sQuery(id+"F11.wireOp",EDGE,"E26.left"),sQuery(id+"F11.wireOp",EDGE,"E26.right")])],"isStart":true})]});
            var Q1;
            Q1=makeQuery(id+"F12.boolean.opBoolean","INTERSECT",EDGE,{"derivedFrom":[makeQuery(id+"F9.opExtrude","CAP_FACE",FACE,{"disambiguationData":[OSD([sQuery(id+"F8.wireOp",EDGE,"E19.MirrorCS"),sQuery(id+"F8.wireOp",EDGE,"E20.MirrorCS"),sQuery(id+"F8.wireOp",EDGE,"E21.MirrorCS"),sQuery(id+"F8.wireOp",EDGE,"E22.MirrorCS"),sQuery(id+"F8.wireOp",EDGE,"E23.MirrorC")])],"isStart":false}),makeQuery(id+"F12.opExtrude","CAP_FACE",FACE,{"disambiguationData":[OSD([sQuery(id+"F11.wireOp",EDGE,"E27.MirrorCS"),sQuery(id+"F11.wireOp",EDGE,"E28.MirrorCS"),sQuery(id+"F11.wireOp",EDGE,"E29.MirrorCS"),sQuery(id+"F11.wireOp",EDGE,"E30.MirrorCS")])],"isStart":true})]});
            fillet(context, id + "F14", {"entities" : qUnion([Q0, Q1]), "radius" : 7 * mm, "tangentPropagation" : true, "allowEdgeOverflow" : false});
        }
    });
